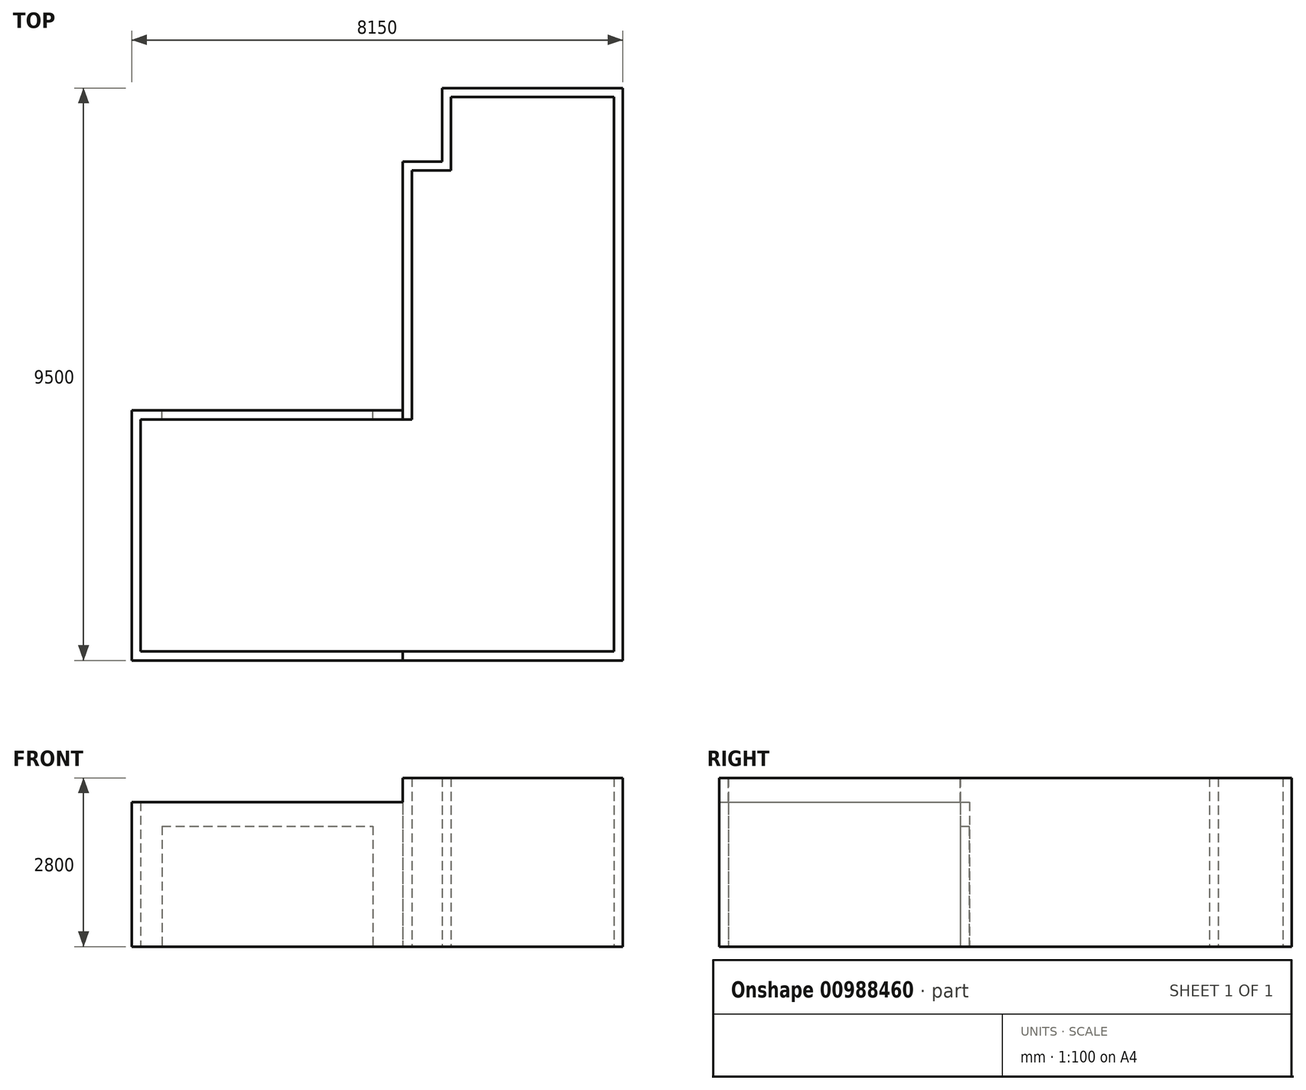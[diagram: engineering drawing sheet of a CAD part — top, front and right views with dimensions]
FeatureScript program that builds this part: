
annotation { "Feature Type Name" : "Feature", "Feature Type Description" : "" }
export const myFeature = defineFeature(function(context is Context, id is Id, definition is map)
    precondition{}
    {
        {
            var Q0;
            Q0=qCreatedBy(makeId("Top.planeOp"),FACE);
            var sketch = newSketch(context, id + "F0", { "sketchPlane" : qUnion([Q0])});
            skLineSegment(sketch, "E0", {"start": v(-1500, 5350) * mm, "end": v(1500, 5350) * mm});
            skLineSegment(sketch, "E1", {"start": v(1500, 5350) * mm, "end": v(1500, -4150) * mm});
            skLineSegment(sketch, "E2", {"start": v(1500, -4150) * mm, "end": v(-6650, -4150) * mm});
            skLineSegment(sketch, "E3", {"start": v(-1500, 5350) * mm, "end": v(-1500, 4130) * mm});
            skLineSegment(sketch, "E4", {"start": v(-1500, 4130) * mm, "end": v(-2150, 4130) * mm});
            skLineSegment(sketch, "E5", {"start": v(-2150, 4130) * mm, "end": v(-2150, 0) * mm});
            skLineSegment(sketch, "E6", {"start": v(-2150, 0) * mm, "end": v(-6650, 0) * mm});
            skLineSegment(sketch, "E7", {"start": v(-6650, 0) * mm, "end": v(-6650, -4150) * mm});
            skLineSegment(sketch, "E8.0", {"start": v(-1350, 5200) * mm, "end": v(-1350, 3980) * mm});
            skLineSegment(sketch, "E8.1", {"start": v(-1350, 3980) * mm, "end": v(-2000, 3980) * mm});
            skLineSegment(sketch, "E8.2", {"start": v(-1350, 5200) * mm, "end": v(1350, 5200) * mm});
            skLineSegment(sketch, "E8.3", {"start": v(-2000, 3980) * mm, "end": v(-2000, -150) * mm});
            skLineSegment(sketch, "E8.4", {"start": v(1350, 5200) * mm, "end": v(1350, -4000) * mm});
            skLineSegment(sketch, "E8.5", {"start": v(1350, -4000) * mm, "end": v(-6500, -4000) * mm});
            skLineSegment(sketch, "E8.6", {"start": v(-6500, -150) * mm, "end": v(-6500, -4000) * mm});
            skLineSegment(sketch, "E8.7", {"start": v(-2000, -150) * mm, "end": v(-6500, -150) * mm});
            skSolve(sketch);
        }
        {
            var Q0;
            Q0=makeQuery(id+"F0.imprint","IMPRINT",FACE,{"disambiguationData":[TD([[makeQuery(id+"F0.imprint","IMPRINT",EDGE,{"derivedFrom":sQuery(id+"F0.wireOp",EDGE,"E0")}),-1.0]])]});
            extrude(context, id + "F1", {"entities" : qUnion([Q0]), "depth" : 2800 * mm, "offsetDistance" : 25 * mm});
        }
        {
            var Q0;
            Q0=makeQuery(id+"F1.opExtrude","SWEPT_FACE",FACE,{"disambiguationData":[OSD([sQuery(id+"F0.wireOp",EDGE,"E6")])]});
            var sketch = newSketch(context, id + "F2", { "sketchPlane" : qUnion([Q0])});
            skLineSegment(sketch, "E9.bottom", {"start": v(2150, 2800) * mm, "end": v(6650, 2800) * mm});
            skLineSegment(sketch, "E9.top", {"start": v(2150, 2400) * mm, "end": v(6650, 2400) * mm});
            skLineSegment(sketch, "E9.left", {"start": v(2150, 2800) * mm, "end": v(2150, 2400) * mm});
            skLineSegment(sketch, "E9.right", {"start": v(6650, 2800) * mm, "end": v(6650, 2400) * mm});
            skSolve(sketch);
        }
        {
            var Q0;
            Q0 = qSketchRegion(id + "F2", true);
            extrude(context, id + "F3", {"entities" : qUnion([Q0]), "operationType" : NewBodyOperationType.REMOVE, "oppositeDirection" : true, "depth" : 4170 * mm, "offsetDistance" : 25 * mm});
        }
        {
            var Q0;
            Q0=makeQuery(id+"F1.opExtrude","SWEPT_FACE",FACE,{"disambiguationData":[OSD([sQuery(id+"F0.wireOp",EDGE,"E6")])]});
            var sketch = newSketch(context, id + "F4", { "sketchPlane" : qUnion([Q0])});
            skLineSegment(sketch, "E10.bottom", {"start": v(2650, 0) * mm, "end": v(6150, 0) * mm});
            skLineSegment(sketch, "E10.top", {"start": v(2650, 2000) * mm, "end": v(6150, 2000) * mm});
            skLineSegment(sketch, "E10.left", {"start": v(2650, 0) * mm, "end": v(2650, 2000) * mm});
            skLineSegment(sketch, "E10.right", {"start": v(6150, 0) * mm, "end": v(6150, 2000) * mm});
            skSolve(sketch);
        }
        {
            var Q0;
            Q0 = qSketchRegion(id + "F4", true);
            extrude(context, id + "F5", {"entities" : qUnion([Q0]), "operationType" : NewBodyOperationType.REMOVE, "oppositeDirection" : true, "depth" : 160 * mm, "offsetDistance" : 25 * mm});
        }
    });
